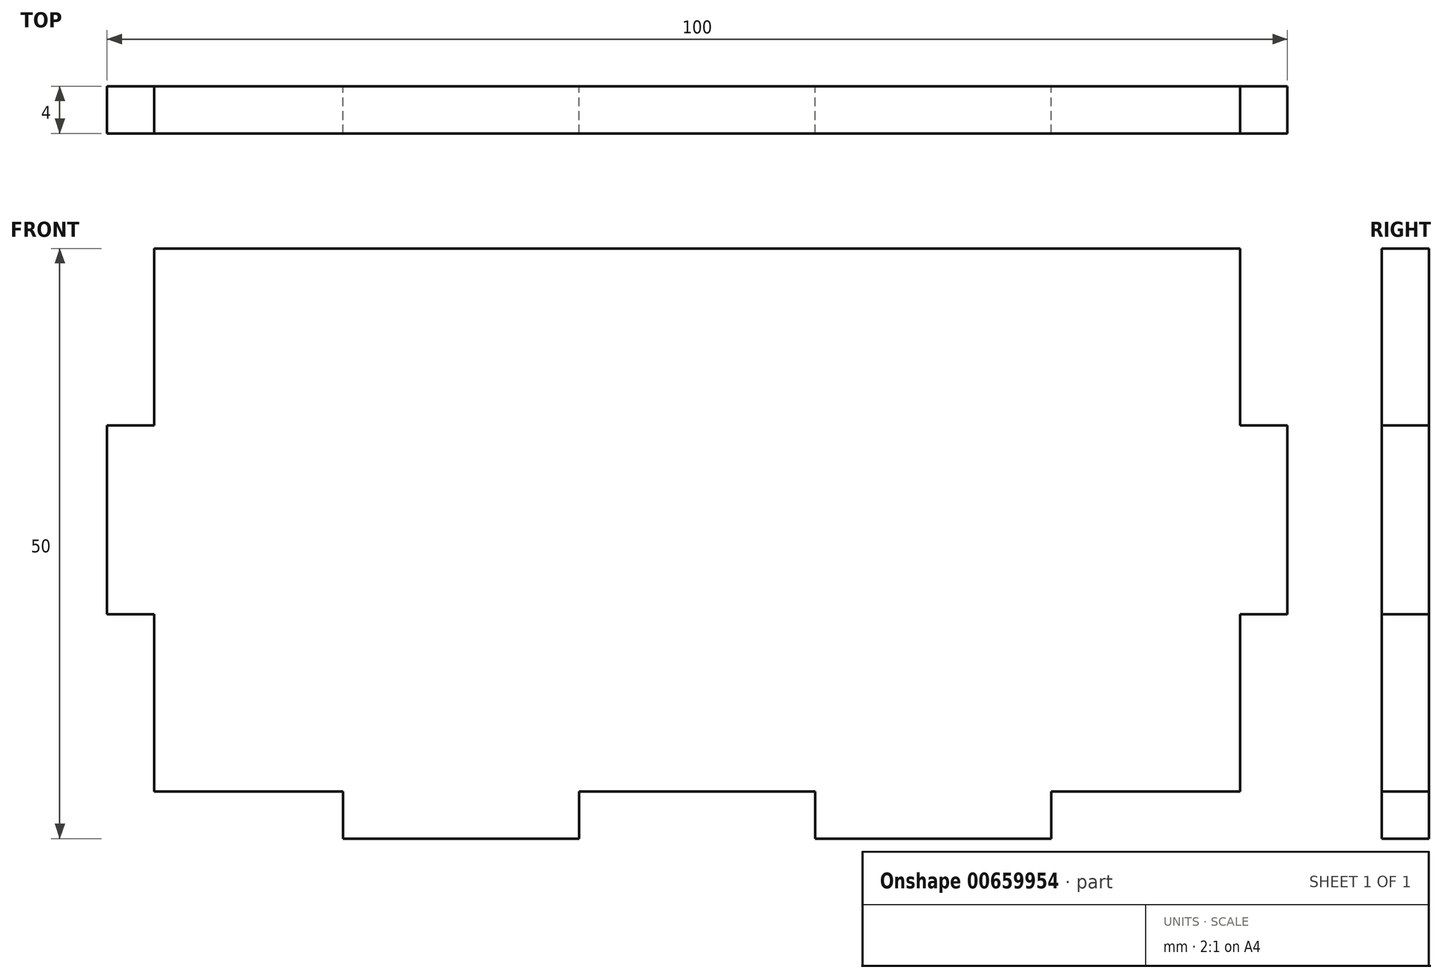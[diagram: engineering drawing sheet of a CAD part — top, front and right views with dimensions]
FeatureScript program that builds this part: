
annotation { "Feature Type Name" : "Feature", "Feature Type Description" : "" }
export const myFeature = defineFeature(function(context is Context, id is Id, definition is map)
    precondition{}
    {
        {
            var Q0;
            Q0=qCreatedBy(makeId("Front.planeOp"),FACE);
            var sketch = newSketch(context, id + "F0", { "sketchPlane" : qUnion([Q0])});
            skLineSegment(sketch, "E0.bottom", {"start": v(-58.47, 63.53) * mm, "end": v(41.53, 63.53) * mm});
            skLineSegment(sketch, "E0.top", {"start": v(-58.47, 13.53) * mm, "end": v(41.53, 13.53) * mm});
            skLineSegment(sketch, "E0.left", {"start": v(-58.47, 63.53) * mm, "end": v(-58.47, 13.53) * mm});
            skLineSegment(sketch, "E0.right", {"start": v(41.53, 63.53) * mm, "end": v(41.53, 13.53) * mm});
            skLineSegment(sketch, "E1.bottom", {"start": v(-58.47, 13.53) * mm, "end": v(-38.47, 13.53) * mm});
            skLineSegment(sketch, "E1.top", {"start": v(-58.47, 17.53) * mm, "end": v(-38.47, 17.53) * mm});
            skLineSegment(sketch, "E1.left", {"start": v(-58.47, 13.53) * mm, "end": v(-58.47, 17.53) * mm});
            skLineSegment(sketch, "E1.right", {"start": v(-38.47, 13.53) * mm, "end": v(-38.47, 17.53) * mm});
            skLineSegment(sketch, "E2.bottom", {"start": v(41.53, 13.53) * mm, "end": v(21.53, 13.53) * mm});
            skLineSegment(sketch, "E2.top", {"start": v(41.53, 17.53) * mm, "end": v(21.53, 17.53) * mm});
            skLineSegment(sketch, "E2.left", {"start": v(41.53, 13.53) * mm, "end": v(41.53, 17.53) * mm});
            skLineSegment(sketch, "E2.right", {"start": v(21.53, 13.53) * mm, "end": v(21.53, 17.53) * mm});
            skLineSegment(sketch, "E3.bottom", {"start": v(1.53, 13.53) * mm, "end": v(-18.47, 13.53) * mm});
            skLineSegment(sketch, "E3.top", {"start": v(1.53, 17.53) * mm, "end": v(-18.47, 17.53) * mm});
            skLineSegment(sketch, "E3.left", {"start": v(1.53, 13.53) * mm, "end": v(1.53, 17.53) * mm});
            skLineSegment(sketch, "E3.right", {"start": v(-18.47, 13.53) * mm, "end": v(-18.47, 17.53) * mm});
            skLineSegment(sketch, "E4.bottom", {"start": v(-58.47, 63.53) * mm, "end": v(-54.47, 63.53) * mm});
            skLineSegment(sketch, "E4.top", {"start": v(-58.47, 48.53) * mm, "end": v(-54.47, 48.53) * mm});
            skLineSegment(sketch, "E4.left", {"start": v(-58.47, 63.53) * mm, "end": v(-58.47, 48.53) * mm});
            skLineSegment(sketch, "E4.right", {"start": v(-54.47, 63.53) * mm, "end": v(-54.47, 48.53) * mm});
            skLineSegment(sketch, "E5.bottom", {"start": v(-58.47, 32.53) * mm, "end": v(-54.47, 32.53) * mm});
            skLineSegment(sketch, "E5.top", {"start": v(-58.47, 17.53) * mm, "end": v(-54.47, 17.53) * mm});
            skLineSegment(sketch, "E5.left", {"start": v(-58.47, 32.53) * mm, "end": v(-58.47, 17.53) * mm});
            skLineSegment(sketch, "E5.right", {"start": v(-54.47, 32.53) * mm, "end": v(-54.47, 17.53) * mm});
            skLineSegment(sketch, "E6.bottom", {"start": v(41.53, 63.53) * mm, "end": v(37.53, 63.53) * mm});
            skLineSegment(sketch, "E6.top", {"start": v(41.53, 48.53) * mm, "end": v(37.53, 48.53) * mm});
            skLineSegment(sketch, "E6.left", {"start": v(41.53, 63.53) * mm, "end": v(41.53, 48.53) * mm});
            skLineSegment(sketch, "E6.right", {"start": v(37.53, 63.53) * mm, "end": v(37.53, 48.53) * mm});
            skLineSegment(sketch, "E7.bottom", {"start": v(41.53, 32.53) * mm, "end": v(37.53, 32.53) * mm});
            skLineSegment(sketch, "E7.top", {"start": v(41.53, 17.53) * mm, "end": v(37.53, 17.53) * mm});
            skLineSegment(sketch, "E7.left", {"start": v(41.53, 32.53) * mm, "end": v(41.53, 17.53) * mm});
            skLineSegment(sketch, "E7.right", {"start": v(37.53, 32.53) * mm, "end": v(37.53, 17.53) * mm});
            skSolve(sketch);
        }
        {
            var Q0;
            {var subQ3=sQuery(id+"F0.wireOp",EDGE,"E1.right");Q0=makeQuery(id+"F0.imprint","IMPRINT",FACE,{"disambiguationData":[TD([[makeQuery(id+"F0.imprint","IMPRINT",EDGE,{"derivedFrom":subQ3}),-1.0]])]});}
            extrude(context, id + "F1", {"entities" : qUnion([Q0]), "depth" : 4 * mm, "offsetDistance" : 25 * mm});
        }
    });
